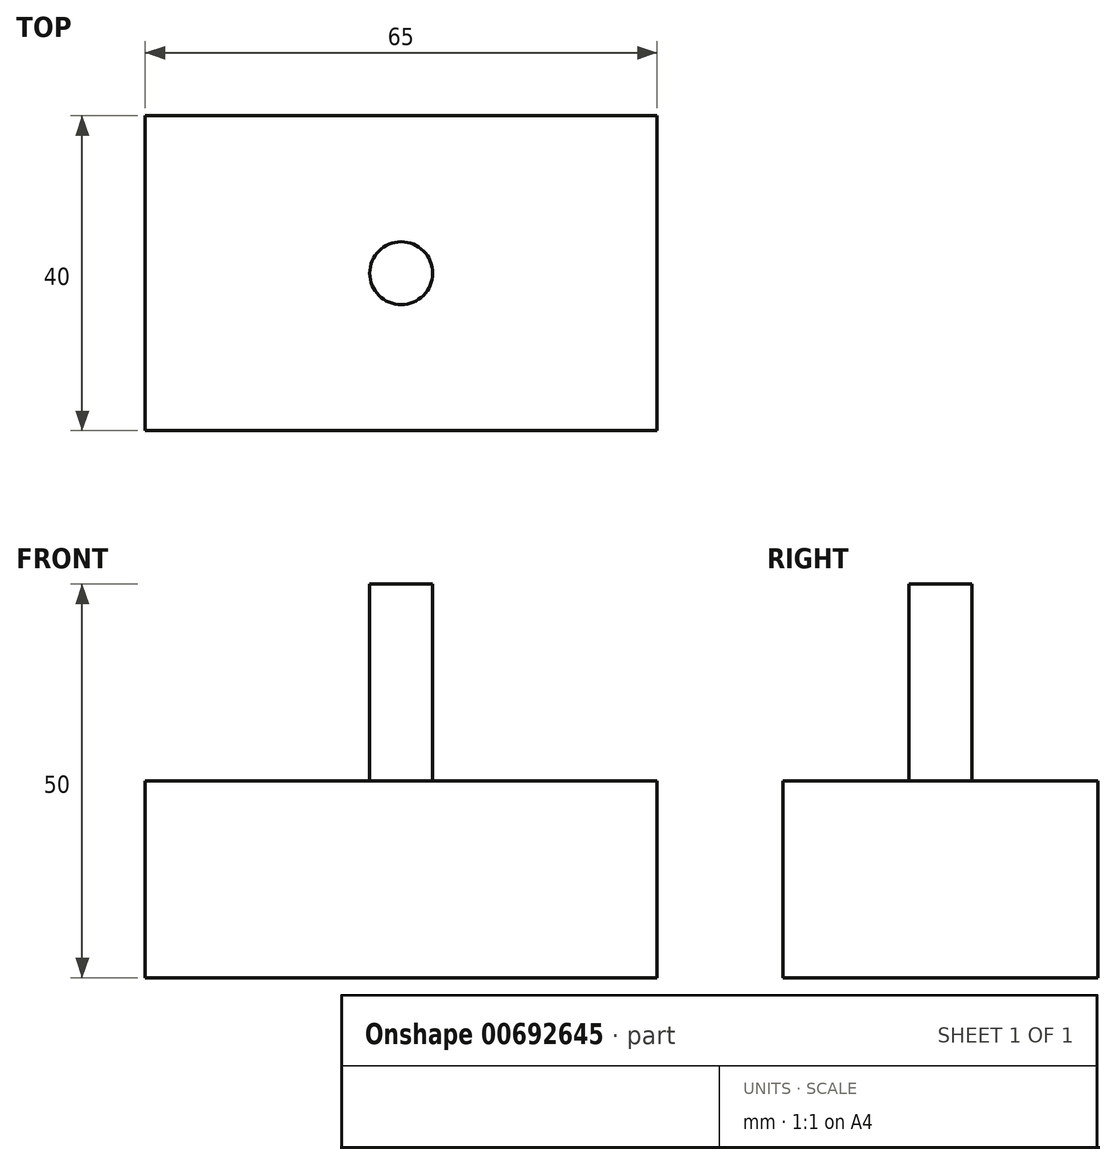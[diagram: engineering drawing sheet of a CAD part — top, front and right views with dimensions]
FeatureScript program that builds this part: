
annotation { "Feature Type Name" : "Feature", "Feature Type Description" : "" }
export const myFeature = defineFeature(function(context is Context, id is Id, definition is map)
    precondition{}
    {
        {
            var Q0;
            Q0=qCreatedBy(makeId("Top.planeOp"),FACE);
            var sketch = newSketch(context, id + "F0", { "sketchPlane" : qUnion([Q0])});
            skLineSegment(sketch, "E0.bottom", {"start": v(-20.5, 0.56) * mm, "end": v(-85.5, 0.56) * mm});
            skLineSegment(sketch, "E0.top", {"start": v(-20.5, 40.56) * mm, "end": v(-85.5, 40.56) * mm});
            skLineSegment(sketch, "E0.left", {"start": v(-20.5, 0.56) * mm, "end": v(-20.5, 40.56) * mm});
            skLineSegment(sketch, "E0.right", {"start": v(-85.5, 0.56) * mm, "end": v(-85.5, 40.56) * mm});
            skPoint(sketch, "E0.middle", {"position": v(-53, 20.56) * mm});
            skSolve(sketch);
        }
        {
            var Q0;
            Q0 = qSketchRegion(id + "F0", true);
            extrude(context, id + "F1", {"entities" : qUnion([Q0]), "depth" : 25 * mm, "offsetDistance" : 25 * mm});
        }
        {
            var Q0;
            Q0=makeQuery(id+"F1.opExtrude","CAP_FACE",FACE,{"disambiguationData":[OSD([sQuery(id+"F0.wireOp",EDGE,"E0.bottom"),sQuery(id+"F0.wireOp",EDGE,"E0.top"),sQuery(id+"F0.wireOp",EDGE,"E0.left"),sQuery(id+"F0.wireOp",EDGE,"E0.right")])],"isStart":false});
            var sketch = newSketch(context, id + "F2", { "sketchPlane" : qUnion([Q0])});
            skCircle(sketch, "E1", {"center": v(-53, 20.56) * mm, "radius": 4 * mm});
            skPoint(sketch, "E1.centerSnap0", {"position": v(-85.5, 20.56) * mm});
            skPoint(sketch, "E1.centerSnap1", {"position": v(-53, 40.56) * mm});
            skSolve(sketch);
        }
        {
            var Q0;
            Q0=makeQuery(id+"F2.imprint","IMPRINT",FACE,{"disambiguationData":[TD([[makeQuery(id+"F2.imprint","IMPRINT",EDGE,{"derivedFrom":sQuery(id+"F2.wireOp",EDGE,"E1")}),1.0]])]});
            extrude(context, id + "F3", {"entities" : qUnion([Q0]), "operationType" : NewBodyOperationType.ADD, "depth" : 25 * mm, "offsetDistance" : 25 * mm});
        }
    });
